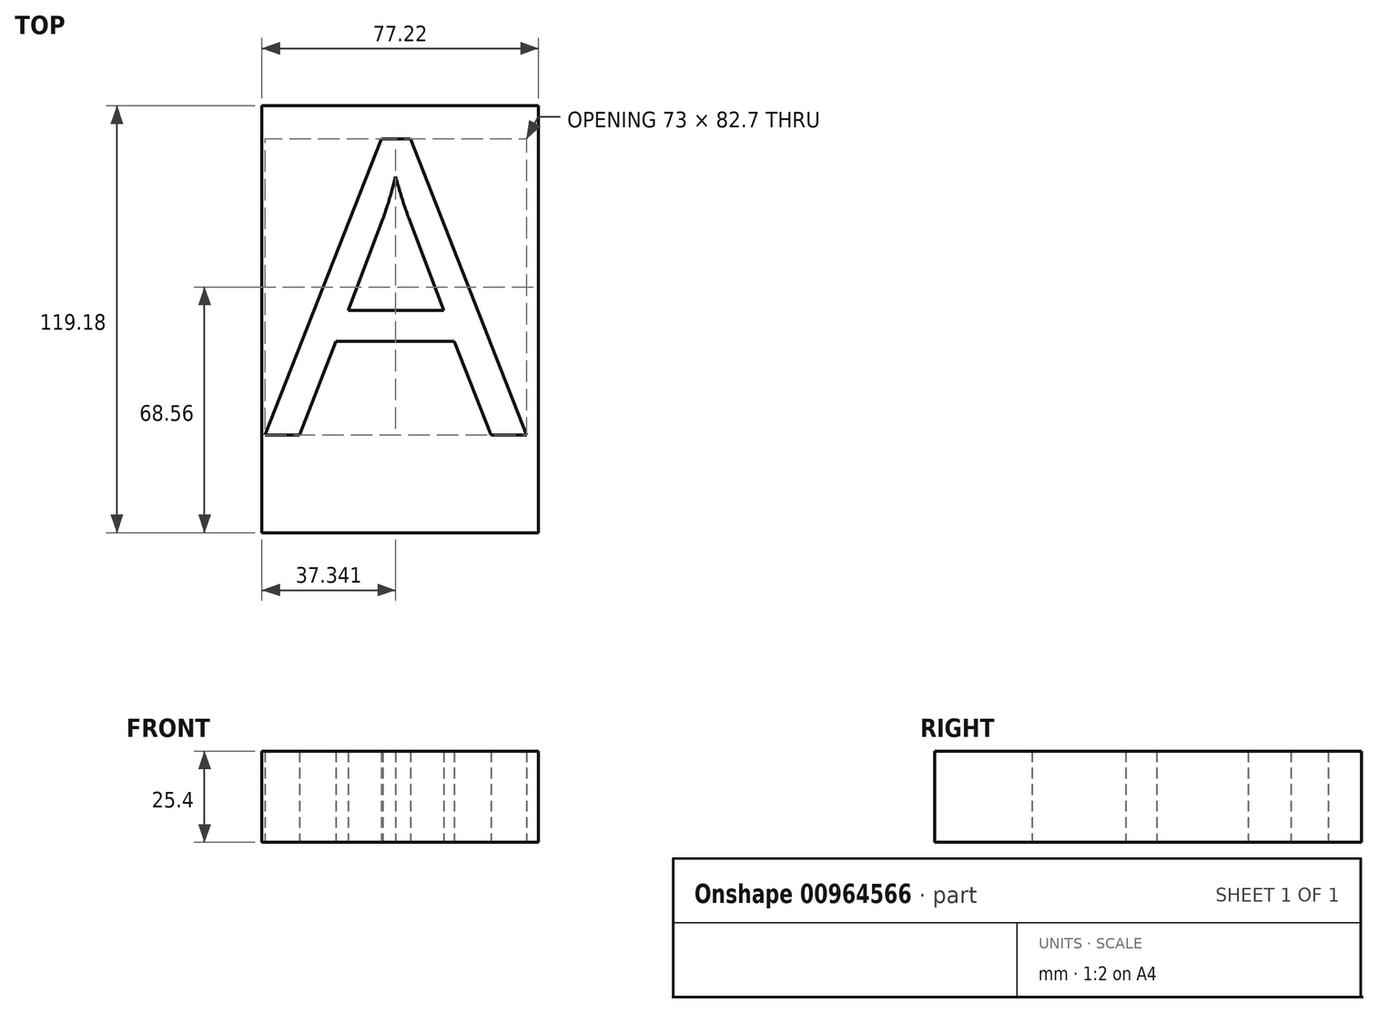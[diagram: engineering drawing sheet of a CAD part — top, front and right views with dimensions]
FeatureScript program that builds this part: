
annotation { "Feature Type Name" : "Feature", "Feature Type Description" : "" }
export const myFeature = defineFeature(function(context is Context, id is Id, definition is map)
    precondition{}
    {
        {
            var Q0;
            Q0=qCreatedBy(makeId("Top.planeOp"),FACE);
            var sketch = newSketch(context, id + "F0", { "sketchPlane" : qUnion([Q0])});
            skLineSegment(sketch, "E0.bottom", {"start": v(38.61, -59.6) * mm, "end": v(-38.61, -59.6) * mm});
            skLineSegment(sketch, "E0.top", {"start": v(38.61, 59.6) * mm, "end": v(-38.61, 59.6) * mm});
            skLineSegment(sketch, "E0.left", {"start": v(38.61, -59.6) * mm, "end": v(38.61, 59.6) * mm});
            skLineSegment(sketch, "E0.right", {"start": v(-38.61, -59.6) * mm, "end": v(-38.61, 59.6) * mm});
            skPoint(sketch, "E0.middle", {"position": v(0, 0) * mm});
            skSolve(sketch);
        }
        {
            var Q0;
            Q0 = qSketchRegion(id + "F0", true);
            extrude(context, id + "F1", {"entities" : qUnion([Q0]), "depth" : 25.4 * mm, "offsetDistance" : 25.4 * mm});
        }
        {
            var Q0;
            Q0=qCreatedBy(makeId("Top.planeOp"),FACE);
            var sketch = newSketch(context, id + "F2", { "sketchPlane" : qUnion([Q0])});
            skText(sketch, "E1", { "text": "A", "fontName": "OpenSans-Regular.ttf"});
            const initialGuessF2  = {"E1": [-0.03777, -0.03238, 1, 0, 0.08306]};
            skSetInitialGuess(sketch, initialGuessF2);
            skSolve(sketch);
        }
        {
            var Q0;
            Q0 = qSketchRegion(id + "F2", true);
            extrude(context, id + "F3", {"entities" : qUnion([Q0]), "operationType" : NewBodyOperationType.REMOVE, "depth" : 25.4 * mm, "offsetDistance" : 25.4 * mm});
        }
    });
